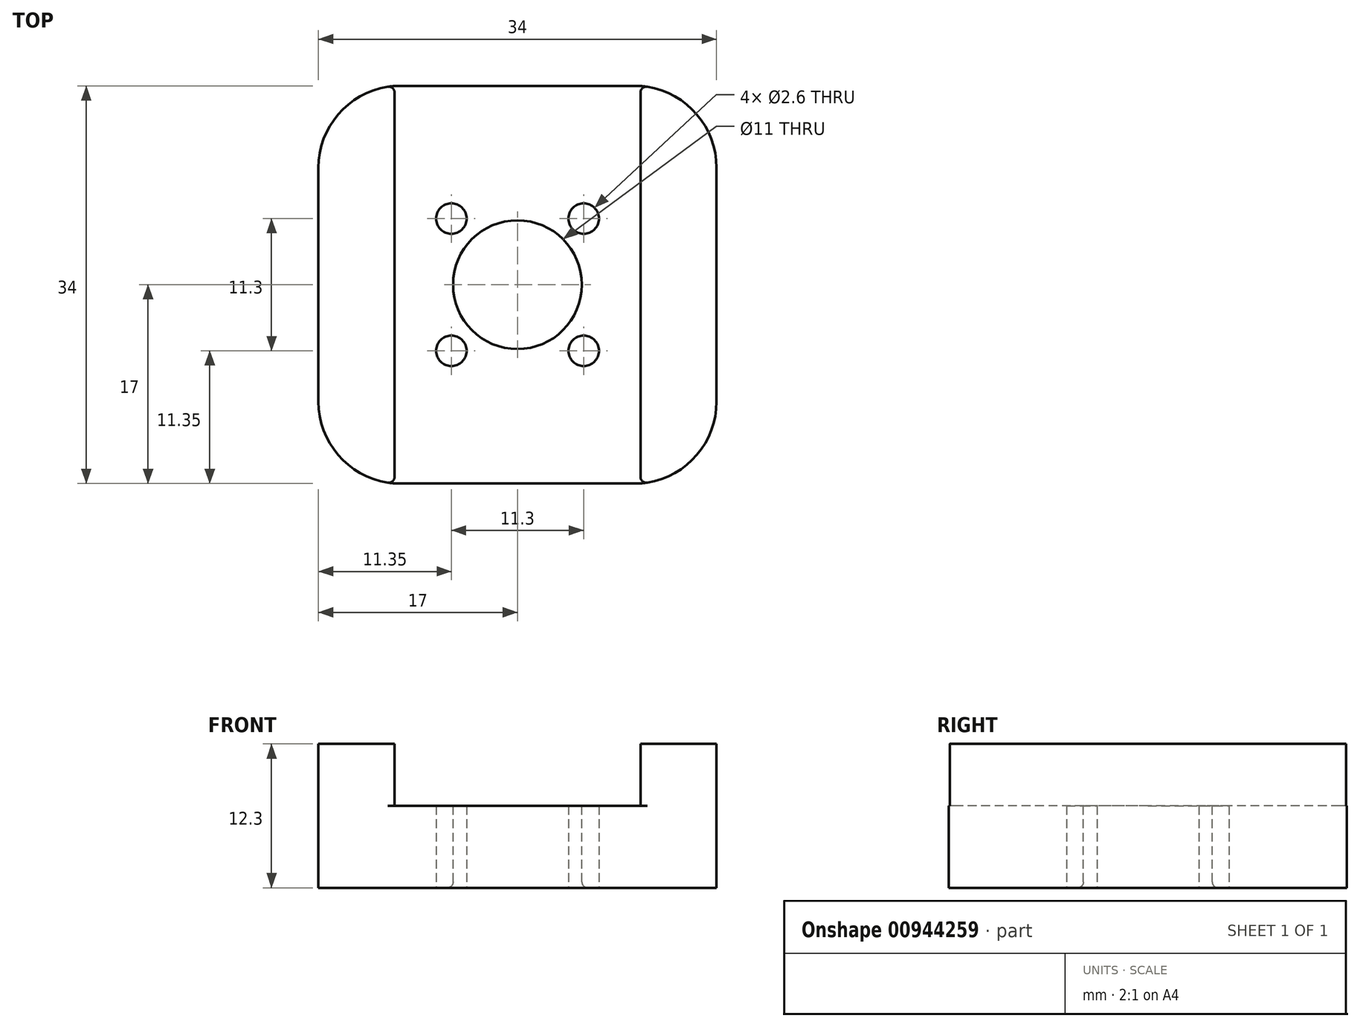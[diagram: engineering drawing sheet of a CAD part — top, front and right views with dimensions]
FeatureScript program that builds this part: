
annotation { "Feature Type Name" : "Feature", "Feature Type Description" : "" }
export const myFeature = defineFeature(function(context is Context, id is Id, definition is map)
    precondition{}
    {
        {
            var Q0;
            Q0=qCreatedBy(makeId("Top.planeOp"),FACE);
            var sketch = newSketch(context, id + "F0", { "sketchPlane" : qUnion([Q0])});
            skLineSegment(sketch, "E0.bottom", {"start": v(-17, 17) * mm, "end": v(17, 17) * mm});
            skLineSegment(sketch, "E0.top", {"start": v(-17, -17) * mm, "end": v(17, -17) * mm});
            skLineSegment(sketch, "E0.left", {"start": v(-17, 17) * mm, "end": v(-17, -17) * mm});
            skLineSegment(sketch, "E0.right", {"start": v(17, 17) * mm, "end": v(17, -17) * mm});
            skPoint(sketch, "E1", {"position": v(0, 17) * mm});
            skPoint(sketch, "E2", {"position": v(17, 0) * mm});
            skSolve(sketch);
        }
        {
            var Q0;
            Q0=qSketchRegion(id+"F0",true);
            extrude(context, id + "F1", {"entities" : qUnion([Q0]), "depth" : 12.3 * mm, "offsetDistance" : 25 * mm});
        }
        {
            var Q0;
            Q0=makeQuery(id+"F1.opExtrude","CAP_FACE",FACE,{"disambiguationData":[OSD([sQuery(id+"F0.wireOp",EDGE,"E0.bottom"),sQuery(id+"F0.wireOp",EDGE,"E0.top"),sQuery(id+"F0.wireOp",EDGE,"E0.left"),sQuery(id+"F0.wireOp",EDGE,"E0.right")])],"isStart":false});
            var sketch = newSketch(context, id + "F2", { "sketchPlane" : qUnion([Q0])});
            skCircle(sketch, "E3", {"center": v(0, 0) * mm, "radius": 5.5 * mm});
            skSolve(sketch);
        }
        {
            var Q0;
            Q0=qSketchRegion(id+"F2",true);
            extrude(context, id + "F3", {"entities" : qUnion([Q0]), "operationType" : NewBodyOperationType.REMOVE, "endBound" : BoundingType.THROUGH_ALL, "oppositeDirection" : true, "depth" : 25 * mm, "offsetDistance" : 25 * mm});
        }
        {
            var Q0;
            Q0=makeQuery(id+"F1.opExtrude","CAP_FACE",FACE,{"disambiguationData":[OSD([sQuery(id+"F0.wireOp",EDGE,"E0.bottom"),sQuery(id+"F0.wireOp",EDGE,"E0.top"),sQuery(id+"F0.wireOp",EDGE,"E0.left"),sQuery(id+"F0.wireOp",EDGE,"E0.right")])],"isStart":true});
            var sketch = newSketch(context, id + "F4", { "sketchPlane" : qUnion([Q0])});
            skCircle(sketch, "E4", {"center": v(-5.65, 5.65) * mm, "radius": 1.3 * mm});
            skCircle(sketch, "E5.0.1.0", {"center": v(-5.65, -5.65) * mm, "radius": 1.3 * mm});
            skCircle(sketch, "E5.1.0.0", {"center": v(5.65, 5.65) * mm, "radius": 1.3 * mm});
            skCircle(sketch, "E5.1.1.0", {"center": v(5.65, -5.65) * mm, "radius": 1.3 * mm});
            skLineSegment(sketch, "E5.direction1", {"start": v(-5.65, 5.65) * mm, "end": v(5.65, 5.65) * mm, "construction": true});
            skLineSegment(sketch, "E5.direction2", {"start": v(-5.65, 5.65) * mm, "end": v(-5.65, -5.65) * mm, "construction": true});
            skSolve(sketch);
        }
        {
            var Q0;
            Q0=qSketchRegion(id+"F4",true);
            extrude(context, id + "F5", {"entities" : qUnion([Q0]), "operationType" : NewBodyOperationType.REMOVE, "endBound" : BoundingType.THROUGH_ALL, "oppositeDirection" : true, "depth" : 25 * mm, "offsetDistance" : 25 * mm});
        }
        {
            var Q0;
            Q0=makeQuery(id+"F1.opExtrude","SWEPT_FACE",FACE,{"disambiguationData":[OSD([sQuery(id+"F0.wireOp",EDGE,"E0.top")])]});
            var sketch = newSketch(context, id + "F6", { "sketchPlane" : qUnion([Q0])});
            skLineSegment(sketch, "E6.bottom", {"start": v(-10.5, 12.3) * mm, "end": v(10.5, 12.3) * mm});
            skLineSegment(sketch, "E6.top", {"start": v(-10.5, 7) * mm, "end": v(10.5, 7) * mm});
            skLineSegment(sketch, "E6.left", {"start": v(-10.5, 12.3) * mm, "end": v(-10.5, 7) * mm});
            skLineSegment(sketch, "E6.right", {"start": v(10.5, 12.3) * mm, "end": v(10.5, 7) * mm});
            skPoint(sketch, "E7", {"position": v(0, 7) * mm});
            skSolve(sketch);
        }
        {
            var Q0;
            Q0=qSketchRegion(id+"F6",true);
            extrude(context, id + "F7", {"entities" : qUnion([Q0]), "operationType" : NewBodyOperationType.REMOVE, "endBound" : BoundingType.THROUGH_ALL, "oppositeDirection" : true, "depth" : 25 * mm, "offsetDistance" : 25 * mm});
        }
        {
            var Q0;
            Q0=makeQuery(id+"F1.opExtrude","SWEPT_EDGE",EDGE,{"disambiguationData":[OSD([sQuery(id+"F0.wireOp",EDGE,"E0.top"),sQuery(id+"F0.wireOp",EDGE,"E0.left")])]});
            var Q1;
            Q1=makeQuery(id+"F1.opExtrude","SWEPT_EDGE",EDGE,{"disambiguationData":[OSD([sQuery(id+"F0.wireOp",EDGE,"E0.top"),sQuery(id+"F0.wireOp",EDGE,"E0.right")])]});
            var Q2;
            Q2=makeQuery(id+"F1.opExtrude","SWEPT_EDGE",EDGE,{"disambiguationData":[OSD([sQuery(id+"F0.wireOp",EDGE,"E0.bottom"),sQuery(id+"F0.wireOp",EDGE,"E0.right")])]});
            var Q3;
            Q3=makeQuery(id+"F1.opExtrude","SWEPT_EDGE",EDGE,{"disambiguationData":[OSD([sQuery(id+"F0.wireOp",EDGE,"E0.bottom"),sQuery(id+"F0.wireOp",EDGE,"E0.left")])]});
            fillet(context, id + "F8", {"entities" : qUnion([Q0, Q1, Q2, Q3]), "radius" : 7 * mm, "tangentPropagation" : true, "allowEdgeOverflow" : false});
        }
        {
            var Q0;
            Q0=makeQuery(id+"F3.boolean.opBoolean","INTERSECT",EDGE,{"derivedFrom":[makeQuery(id+"F1.opExtrude","CAP_FACE",FACE,{"disambiguationData":[OSD([sQuery(id+"F0.wireOp",EDGE,"E0.bottom"),sQuery(id+"F0.wireOp",EDGE,"E0.top"),sQuery(id+"F0.wireOp",EDGE,"E0.left"),sQuery(id+"F0.wireOp",EDGE,"E0.right")])],"isStart":true}),makeQuery(id+"F3.opExtrude","SWEPT_FACE",FACE,{"disambiguationData":[OSD([sQuery(id+"F2.wireOp",EDGE,"E3")])]})]});
            var Q1;
            Q1=makeQuery(id+"F8.opFillet","BLEND_EDGE",EDGE,{"blendedFrom":[makeQuery(id+"F1.opExtrude","SWEPT_EDGE",EDGE,{"disambiguationData":[OSD([sQuery(id+"F0.wireOp",EDGE,"E0.bottom"),sQuery(id+"F0.wireOp",EDGE,"E0.left")])]}),makeQuery(id+"F7.boolean.opBoolean","COPY",FACE,{"derivedFrom":makeQuery(id+"F7.opExtrude","SWEPT_FACE",FACE,{"disambiguationData":[OSD([sQuery(id+"F6.wireOp",EDGE,"E6.left")])]})})],"blendedInto":[makeQuery(id+"F7.boolean.opBoolean","COPY",FACE,{"derivedFrom":makeQuery(id+"F7.opExtrude","SWEPT_FACE",FACE,{"disambiguationData":[OSD([sQuery(id+"F6.wireOp",EDGE,"E6.left")])]})})]});
            var Q2;
            Q2=makeQuery(id+"F8.opFillet","BLEND_EDGE",EDGE,{"blendedFrom":[makeQuery(id+"F1.opExtrude","SWEPT_EDGE",EDGE,{"disambiguationData":[OSD([sQuery(id+"F0.wireOp",EDGE,"E0.top"),sQuery(id+"F0.wireOp",EDGE,"E0.left")])]}),makeQuery(id+"F7.boolean.opBoolean","COPY",FACE,{"derivedFrom":makeQuery(id+"F7.opExtrude","SWEPT_FACE",FACE,{"disambiguationData":[OSD([sQuery(id+"F6.wireOp",EDGE,"E6.left")])]})})],"blendedInto":[makeQuery(id+"F7.boolean.opBoolean","COPY",FACE,{"derivedFrom":makeQuery(id+"F7.opExtrude","SWEPT_FACE",FACE,{"disambiguationData":[OSD([sQuery(id+"F6.wireOp",EDGE,"E6.left")])]})})]});
            var Q3;
            Q3=makeQuery(id+"F8.opFillet","BLEND_EDGE",EDGE,{"blendedFrom":[makeQuery(id+"F1.opExtrude","SWEPT_EDGE",EDGE,{"disambiguationData":[OSD([sQuery(id+"F0.wireOp",EDGE,"E0.top"),sQuery(id+"F0.wireOp",EDGE,"E0.right")])]}),makeQuery(id+"F7.boolean.opBoolean","COPY",FACE,{"derivedFrom":makeQuery(id+"F7.opExtrude","SWEPT_FACE",FACE,{"disambiguationData":[OSD([sQuery(id+"F6.wireOp",EDGE,"E6.right")])]})})],"blendedInto":[makeQuery(id+"F7.boolean.opBoolean","COPY",FACE,{"derivedFrom":makeQuery(id+"F7.opExtrude","SWEPT_FACE",FACE,{"disambiguationData":[OSD([sQuery(id+"F6.wireOp",EDGE,"E6.right")])]})})]});
            var Q4;
            Q4=makeQuery(id+"F8.opFillet","BLEND_EDGE",EDGE,{"blendedFrom":[makeQuery(id+"F1.opExtrude","SWEPT_EDGE",EDGE,{"disambiguationData":[OSD([sQuery(id+"F0.wireOp",EDGE,"E0.bottom"),sQuery(id+"F0.wireOp",EDGE,"E0.right")])]}),makeQuery(id+"F7.boolean.opBoolean","COPY",FACE,{"derivedFrom":makeQuery(id+"F7.opExtrude","SWEPT_FACE",FACE,{"disambiguationData":[OSD([sQuery(id+"F6.wireOp",EDGE,"E6.right")])]})})],"blendedInto":[makeQuery(id+"F7.boolean.opBoolean","COPY",FACE,{"derivedFrom":makeQuery(id+"F7.opExtrude","SWEPT_FACE",FACE,{"disambiguationData":[OSD([sQuery(id+"F6.wireOp",EDGE,"E6.right")])]})})]});
            fillet(context, id + "F9", {"entities" : qUnion([Q0, Q1, Q2, Q3, Q4]), "radius" : 0.5 * mm, "tangentPropagation" : true, "allowEdgeOverflow" : false});
        }
    });
